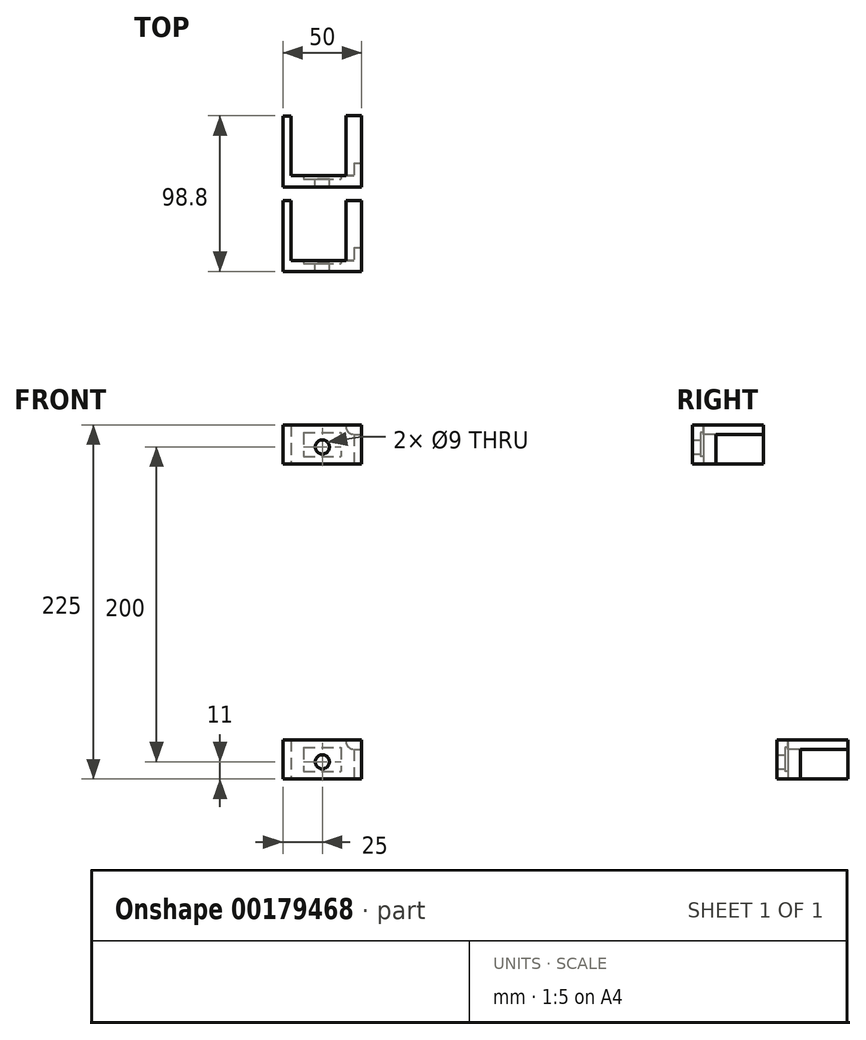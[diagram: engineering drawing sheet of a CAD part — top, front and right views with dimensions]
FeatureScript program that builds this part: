
annotation { "Feature Type Name" : "Feature", "Feature Type Description" : "" }
export const myFeature = defineFeature(function(context is Context, id is Id, definition is map)
    precondition{}
    {
        {
            var Q0;
            Q0=qCreatedBy(makeId("Top.planeOp"),FACE);
            var sketch = newSketch(context, id + "F0", { "sketchPlane" : qUnion([Q0])});
            skLineSegment(sketch, "E0.bottom", {"start": v(0, 0) * mm, "end": v(50, 0) * mm});
            skLineSegment(sketch, "E0.top", {"start": v(0, 15) * mm, "end": v(50, 15) * mm});
            skLineSegment(sketch, "E0.left", {"start": v(0, 0) * mm, "end": v(0, 15) * mm});
            skLineSegment(sketch, "E0.right", {"start": v(50, 0) * mm, "end": v(50, 15) * mm});
            skLineSegment(sketch, "E1.bottom", {"start": v(5, 15) * mm, "end": v(45, 15) * mm});
            skLineSegment(sketch, "E1.top", {"start": v(5, 5) * mm, "end": v(45, 5) * mm});
            skLineSegment(sketch, "E1.left", {"start": v(5, 15) * mm, "end": v(5, 5) * mm});
            skLineSegment(sketch, "E1.right", {"start": v(45, 15) * mm, "end": v(45, 5) * mm});
            skLineSegment(sketch, "E2.bottom", {"start": v(0, 15) * mm, "end": v(5, 15) * mm, "construction": true});
            skLineSegment(sketch, "E2.top", {"start": v(0, 45) * mm, "end": v(5, 45) * mm});
            skLineSegment(sketch, "E2.left", {"start": v(0, 15) * mm, "end": v(0, 45) * mm});
            skLineSegment(sketch, "E2.right", {"start": v(5, 15) * mm, "end": v(5, 45) * mm});
            skSolve(sketch);
        }
        {
            var Q0;
            Q0=makeQuery(id+"F0.imprint","IMPRINT",FACE,{"disambiguationData":[TD([[makeQuery(id+"F0.imprint","IMPRINT",EDGE,{"derivedFrom":sQuery(id+"F0.wireOp",EDGE,"E0.bottom")}),1.0]])]});
            var Q1;
            Q1=makeQuery(id+"F0.imprint","IMPRINT",FACE,{"disambiguationData":[TD([[makeQuery(id+"F0.imprint","IMPRINT",EDGE,{"derivedFrom":sQuery(id+"F0.wireOp",EDGE,"E2.top")}),-1.0]])]});
            extrude(context, id + "F1", {"entities" : qUnion([Q0, Q1]), "depth" : 25 * mm});
        }
        {
            var Q0;
            Q0=makeQuery(id+"F1.opExtrude","CAP_FACE",FACE,{"disambiguationData":[OSD([sQuery(id+"F0.wireOp",EDGE,"E0.bottom"),sQuery(id+"F0.wireOp",EDGE,"E0.top"),sQuery(id+"F0.wireOp",EDGE,"E0.left"),sQuery(id+"F0.wireOp",EDGE,"E0.right"),sQuery(id+"F0.wireOp",EDGE,"E1.top"),sQuery(id+"F0.wireOp",EDGE,"E1.left"),sQuery(id+"F0.wireOp",EDGE,"E1.right"),sQuery(id+"F0.wireOp",EDGE,"E2.top"),sQuery(id+"F0.wireOp",EDGE,"E2.left"),sQuery(id+"F0.wireOp",EDGE,"E2.right")])],"isStart":false});
            var sketch = newSketch(context, id + "F2", { "sketchPlane" : qUnion([Q0])});
            skLineSegment(sketch, "E3.bottom", {"start": v(45, 15) * mm, "end": v(50, 15) * mm});
            skLineSegment(sketch, "E3.top", {"start": v(45, 25) * mm, "end": v(50, 25) * mm});
            skLineSegment(sketch, "E3.left", {"start": v(45, 15) * mm, "end": v(45, 25) * mm});
            skLineSegment(sketch, "E3.right", {"start": v(50, 15) * mm, "end": v(50, 25) * mm});
            skSolve(sketch);
        }
        {
            var Q0;
            Q0=makeQuery(id+"F2.imprint","IMPRINT",FACE,{"disambiguationData":[TD([[makeQuery(id+"F2.imprint","IMPRINT",EDGE,{"derivedFrom":sQuery(id+"F2.wireOp",EDGE,"E3.bottom")}),1.0]])]});
            var Q1;
            Q1=makeQuery(id+"F2.imprint","IMPRINT",FACE,{"disambiguationData":[TD([[makeQuery(id+"F2.imprint","IMPRINT",EDGE,{"derivedFrom":sQuery(id+"F2.wireOp",EDGE,"tBBVbf9j-1Bub-xiSX-YG8x-8XV0MHuePTg5.bottom")}),-1.0]])]});
            extrude(context, id + "F3", {"entities" : qUnion([Q0, Q1]), "operationType" : NewBodyOperationType.ADD, "oppositeDirection" : true, "depth" : 5 * mm});
        }
        {
            var Q0;
            Q0=makeQuery(id+"F1.opExtrude","SWEPT_FACE",FACE,{"disambiguationData":[OSD([sQuery(id+"F0.wireOp",EDGE,"E1.top")])]});
            var sketch = newSketch(context, id + "F4", { "sketchPlane" : qUnion([Q0])});
            skLineSegment(sketch, "E4.bottom", {"start": v(-5, 0) * mm, "end": v(-45, 0) * mm});
            skLineSegment(sketch, "E4.top", {"start": v(-5, 25) * mm, "end": v(-45, 25) * mm});
            skLineSegment(sketch, "E4.left", {"start": v(-5, 0) * mm, "end": v(-5, 25) * mm});
            skLineSegment(sketch, "E4.right", {"start": v(-45, 0) * mm, "end": v(-45, 25) * mm});
            skLineSegment(sketch, "E5.bottom", {"start": v(-5, 25) * mm, "end": v(-13, 25) * mm, "construction": true});
            skLineSegment(sketch, "E5.top", {"start": v(-5, 20) * mm, "end": v(-13, 20) * mm, "construction": true});
            skLineSegment(sketch, "E5.left", {"start": v(-5, 25) * mm, "end": v(-5, 20) * mm, "construction": true});
            skLineSegment(sketch, "E5.right", {"start": v(-13, 25) * mm, "end": v(-13, 20) * mm, "construction": true});
            skLineSegment(sketch, "E6.bottom", {"start": v(-45, 0) * mm, "end": v(-37, 0) * mm, "construction": true});
            skLineSegment(sketch, "E6.top", {"start": v(-45, 5) * mm, "end": v(-37, 5) * mm, "construction": true});
            skLineSegment(sketch, "E6.left", {"start": v(-45, 0) * mm, "end": v(-45, 5) * mm, "construction": true});
            skLineSegment(sketch, "E6.right", {"start": v(-37, 0) * mm, "end": v(-37, 5) * mm, "construction": true});
            skLineSegment(sketch, "E7.bottom", {"start": v(-13, 20) * mm, "end": v(-37, 20) * mm});
            skLineSegment(sketch, "E7.top", {"start": v(-13, 5) * mm, "end": v(-37, 5) * mm});
            skLineSegment(sketch, "E7.left", {"start": v(-13, 20) * mm, "end": v(-13, 5) * mm});
            skLineSegment(sketch, "E7.right", {"start": v(-37, 20) * mm, "end": v(-37, 5) * mm});
            skCircle(sketch, "E8", {"center": v(-25, 11) * mm, "radius": 4.5 * mm});
            skSolve(sketch);
        }
        {
            var Q0;
            Q0=makeQuery(id+"F4.imprint","IMPRINT",FACE,{"disambiguationData":[TD([[makeQuery(id+"F4.imprint","IMPRINT",EDGE,{"derivedFrom":sQuery(id+"F4.wireOp",EDGE,"E4.bottom")}),-1.0]])]});
            extrude(context, id + "F5", {"entities" : qUnion([Q0]), "operationType" : NewBodyOperationType.ADD, "depth" : 2 * mm});
        }
        {
            var Q0;
            Q0=makeQuery(id+"F1.opExtrude","SWEPT_FACE",FACE,{"disambiguationData":[OSD([sQuery(id+"F0.wireOp",EDGE,"E0.left"),sQuery(id+"F0.wireOp",EDGE,"E2.left")])]});
            var sketch = newSketch(context, id + "F6", { "sketchPlane" : qUnion([Q0])});
            skLineSegment(sketch, "E9.bottom", {"start": v(0, 25) * mm, "end": v(-45, 25) * mm});
            skLineSegment(sketch, "E9.top", {"start": v(0, 19) * mm, "end": v(-45, 19) * mm});
            skLineSegment(sketch, "E9.right", {"start": v(-45, 25) * mm, "end": v(-45, 19) * mm});
            skLineSegment(sketch, "E10.top", {"start": v(0, 19) * mm, "end": v(-10, 19) * mm, "construction": true});
            skArc(sketch, "E11", {"start": v(-10, 24) * mm, "mid": v(-6.46, 22.54) * mm, "end": v(-5, 19) * mm});
            skLineSegment(sketch, "E12", {"start": v(-5, 19) * mm, "end": v(-5, 25) * mm});
            skLineSegment(sketch, "E13", {"start": v(-5, 25) * mm, "end": v(-10, 25) * mm});
            skLineSegment(sketch, "E14", {"start": v(0, 19) * mm, "end": v(0, 25) * mm, "construction": true});
            skLineSegment(sketch, "E15", {"start": v(-10, 24) * mm, "end": v(-10, 25) * mm});
            skSolve(sketch);
        }
        {
            var Q0;
            Q0=makeQuery(id+"F6.imprint","IMPRINT",FACE,{"disambiguationData":[TD([[makeQuery(id+"F6.imprint","IMPRINT",EDGE,{"derivedFrom":sQuery(id+"F6.wireOp",EDGE,"E11")}),1.0]])]});
            extrude(context, id + "F7", {"entities" : qUnion([Q0]), "operationType" : NewBodyOperationType.ADD, "oppositeDirection" : true, "depth" : 49 * mm});
        }
        {
            var Q0;
            Q0=makeQuery(id+"F1.opExtrude","SWEPT_FACE",FACE,{"disambiguationData":[OSD([sQuery(id+"F0.wireOp",EDGE,"E0.bottom")])]});
            var sketch = newSketch(context, id + "F8", { "sketchPlane" : qUnion([Q0])});
            skLineSegment(sketch, "E16.bottom", {"start": v(50, 25) * mm, "end": v(45, 25) * mm});
            skLineSegment(sketch, "E16.top", {"start": v(50, 19) * mm, "end": v(45, 19) * mm});
            skLineSegment(sketch, "E16.left", {"start": v(50, 25) * mm, "end": v(50, 19) * mm});
            skLineSegment(sketch, "E16.right", {"start": v(45, 25) * mm, "end": v(45, 19) * mm});
            skLineSegment(sketch, "E17", {"start": v(45, 25) * mm, "end": v(40, 25) * mm});
            skLineSegment(sketch, "E18", {"start": v(45, 25) * mm, "end": v(45, 24) * mm});
            skLineSegment(sketch, "E19", {"start": v(40, 25) * mm, "end": v(40, 24) * mm});
            skLineSegment(sketch, "E20", {"start": v(40, 24) * mm, "end": v(45, 24) * mm});
            skArc(sketch, "E21", {"start": v(40, 24) * mm, "mid": v(41.46, 20.46) * mm, "end": v(45, 19) * mm});
            skSolve(sketch);
        }
        {
            var Q0;
            Q0=makeQuery(id+"F8.imprint","IMPRINT",FACE,{"disambiguationData":[TD([[makeQuery(id+"F8.imprint","IMPRINT",EDGE,{"derivedFrom":sQuery(id+"F8.wireOp",EDGE,"E16.right")}),-1.0]])]});
            var Q1;
            Q1=makeQuery(id+"F8.imprint","IMPRINT",FACE,{"disambiguationData":[TD([[makeQuery(id+"F8.imprint","IMPRINT",EDGE,{"derivedFrom":sQuery(id+"F8.wireOp",EDGE,"E17")}),-1.0]])]});
            var Q2;
            Q2=makeQuery(id+"F8.imprint","IMPRINT",FACE,{"disambiguationData":[TD([[makeQuery(id+"F8.imprint","IMPRINT",EDGE,{"derivedFrom":sQuery(id+"F8.wireOp",EDGE,"E16.bottom")}),-1.0]])]});
            extrude(context, id + "F9", {"entities" : qUnion([Q0, Q1, Q2]), "operationType" : NewBodyOperationType.ADD, "oppositeDirection" : true, "depth" : 45.1 * mm});
        }
        {
            var Q0;
            Q0=makeQuery(id+"F4.imprint","IMPRINT",FACE,{"disambiguationData":[TD([[makeQuery(id+"F4.imprint","IMPRINT",EDGE,{"derivedFrom":sQuery(id+"F4.wireOp",EDGE,"E8")}),1.0]])]});
            extrude(context, id + "F10", {"entities" : qUnion([Q0]), "operationType" : NewBodyOperationType.REMOVE, "oppositeDirection" : true, "depth" : 25 * mm});
        }
        {
            var Q0;
            Q0=makeQuery(id+"F1.opExtrude","SWEPT_BODY",BODY,{"disambiguationData":[OSD([sQuery(id+"F0.wireOp",EDGE,"E0.bottom"),sQuery(id+"F0.wireOp",EDGE,"E0.top"),sQuery(id+"F0.wireOp",EDGE,"E0.left"),sQuery(id+"F0.wireOp",EDGE,"E0.right"),sQuery(id+"F0.wireOp",EDGE,"E1.top"),sQuery(id+"F0.wireOp",EDGE,"E1.left"),sQuery(id+"F0.wireOp",EDGE,"E1.right"),sQuery(id+"F0.wireOp",EDGE,"E2.top"),sQuery(id+"F0.wireOp",EDGE,"E2.left"),sQuery(id+"F0.wireOp",EDGE,"E2.right")])]});
            transform(context, id + "F11", {"entities" : qUnion([Q0]), "transformType" : TransformType.TRANSLATION_3D, "dx" : 0 * mm, "dy" : -53.7 * mm, "dz" : 200 * mm, "makeCopy" : true});
        }
    });
